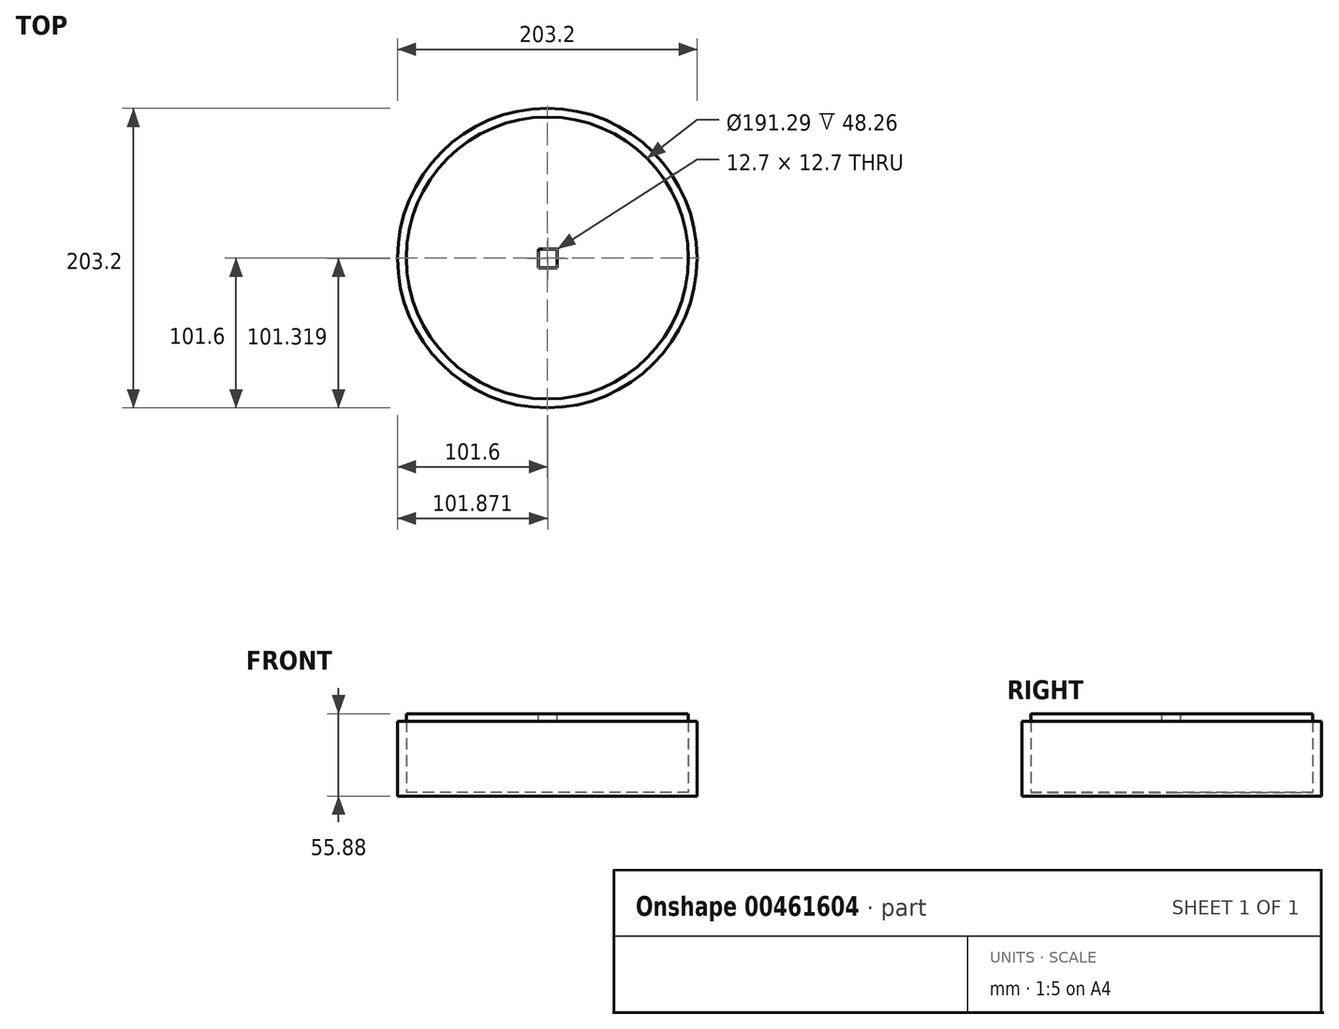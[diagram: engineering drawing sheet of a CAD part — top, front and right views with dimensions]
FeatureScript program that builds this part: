
annotation { "Feature Type Name" : "Feature", "Feature Type Description" : "" }
export const myFeature = defineFeature(function(context is Context, id is Id, definition is map)
    precondition{}
    {
        {
            var Q0;
            Q0=qCreatedBy(makeId("Top.planeOp"),FACE);
            var sketch = newSketch(context, id + "F0", { "sketchPlane" : qUnion([Q0])});
            skCircle(sketch, "E0", {"center": v(0, 0) * mm, "radius": 101.6 * mm});
            skSolve(sketch);
        }
        {
            var Q0;
            Q0=makeQuery(id+"F0.imprint","IMPRINT",FACE,{"disambiguationData":[TD([[makeQuery(id+"F0.imprint","IMPRINT",EDGE,{"derivedFrom":sQuery(id+"F0.wireOp",EDGE,"E0")}),1.0]])]});
            var sketch = newSketch(context, id + "F1", { "sketchPlane" : qUnion([Q0])});
            skCircle(sketch, "E1", {"center": v(0, 0) * mm, "radius": 95.64 * mm});
            skSolve(sketch);
        }
        {
            var Q0;
            Q0=makeQuery(id+"F1.imprint","IMPRINT",FACE,{"disambiguationData":[TD([[makeQuery(id+"F1.imprint","IMPRINT",EDGE,{"derivedFrom":sQuery(id+"F1.wireOp",EDGE,"E1")}),-1.0]])]});
            extrude(context, id + "F2", {"entities" : qUnion([Q0]), "depth" : 50.8 * mm});
        }
        {
            var Q0;
            Q0=makeQuery(id+"F0.imprint","IMPRINT",FACE,{"disambiguationData":[TD([[makeQuery(id+"F0.imprint","IMPRINT",EDGE,{"derivedFrom":sQuery(id+"F0.wireOp",EDGE,"E0")}),1.0]])]});
            var sketch = newSketch(context, id + "F3", { "sketchPlane" : qUnion([Q0])});
            skCircle(sketch, "E2", {"center": v(0, 0) * mm, "radius": 95.67 * mm});
            skSolve(sketch);
        }
        {
            var Q0;
            Q0=makeQuery(id+"F3.imprint","IMPRINT",FACE,{"disambiguationData":[TD([[makeQuery(id+"F3.imprint","IMPRINT",EDGE,{"derivedFrom":sQuery(id+"F3.wireOp",EDGE,"E2")}),1.0]])]});
            extrude(context, id + "F4", {"entities" : qUnion([Q0]), "operationType" : NewBodyOperationType.ADD, "depth" : 2.54 * mm});
        }
        {
            var Q0;
            Q0=makeQuery(id+"F2.opExtrude","CAP_FACE",FACE,{"disambiguationData":[OSD([sQuery(id+"F0.wireOp",EDGE,"E0"),sQuery(id+"F1.wireOp",EDGE,"E1")])],"isStart":false});
            var sketch = newSketch(context, id + "F5", { "sketchPlane" : qUnion([Q0])});
            skCircle(sketch, "E3", {"center": v(0, 0) * mm, "radius": 96.27 * mm});
            skSolve(sketch);
        }
        {
            var Q0;
            Q0=makeQuery(id+"F5.imprint","IMPRINT",FACE,{"disambiguationData":[TD([[makeQuery(id+"F5.imprint","IMPRINT",EDGE,{"derivedFrom":makeQuery(id+"F2.opExtrude","CAP_EDGE",EDGE,{"disambiguationData":[OSD([sQuery(id+"F1.wireOp",EDGE,"E1")])],"isStart":false})}),1.0]])]});
            extrude(context, id + "F6", {"entities" : qUnion([Q0]), "depth" : 5.08 * mm});
        }
        {
            var Q0;
            Q0=makeQuery(id+"F6.opExtrude","CAP_FACE",FACE,{"disambiguationData":[OSD([sQuery(id+"F1.wireOp",EDGE,"E1")])],"isStart":false});
            var sketch = newSketch(context, id + "F7", { "sketchPlane" : qUnion([Q0])});
            skLineSegment(sketch, "E4.bottom", {"start": v(-6.08, 6.07) * mm, "end": v(6.62, 6.07) * mm});
            skLineSegment(sketch, "E4.top", {"start": v(-6.08, -6.63) * mm, "end": v(6.62, -6.63) * mm});
            skLineSegment(sketch, "E4.left", {"start": v(-6.08, 6.07) * mm, "end": v(-6.08, -6.63) * mm});
            skLineSegment(sketch, "E4.right", {"start": v(6.62, 6.07) * mm, "end": v(6.62, -6.63) * mm});
            skSolve(sketch);
        }
        {
            var Q0;
            Q0=makeQuery(id+"F7.imprint","IMPRINT",FACE,{"disambiguationData":[TD([[makeQuery(id+"F7.imprint","IMPRINT",EDGE,{"derivedFrom":sQuery(id+"F7.wireOp",EDGE,"E4.bottom")}),-1.0]])]});
            extrude(context, id + "F8", {"entities" : qUnion([Q0]), "operationType" : NewBodyOperationType.REMOVE, "oppositeDirection" : true, "depth" : 50.8 * mm});
        }
    });
